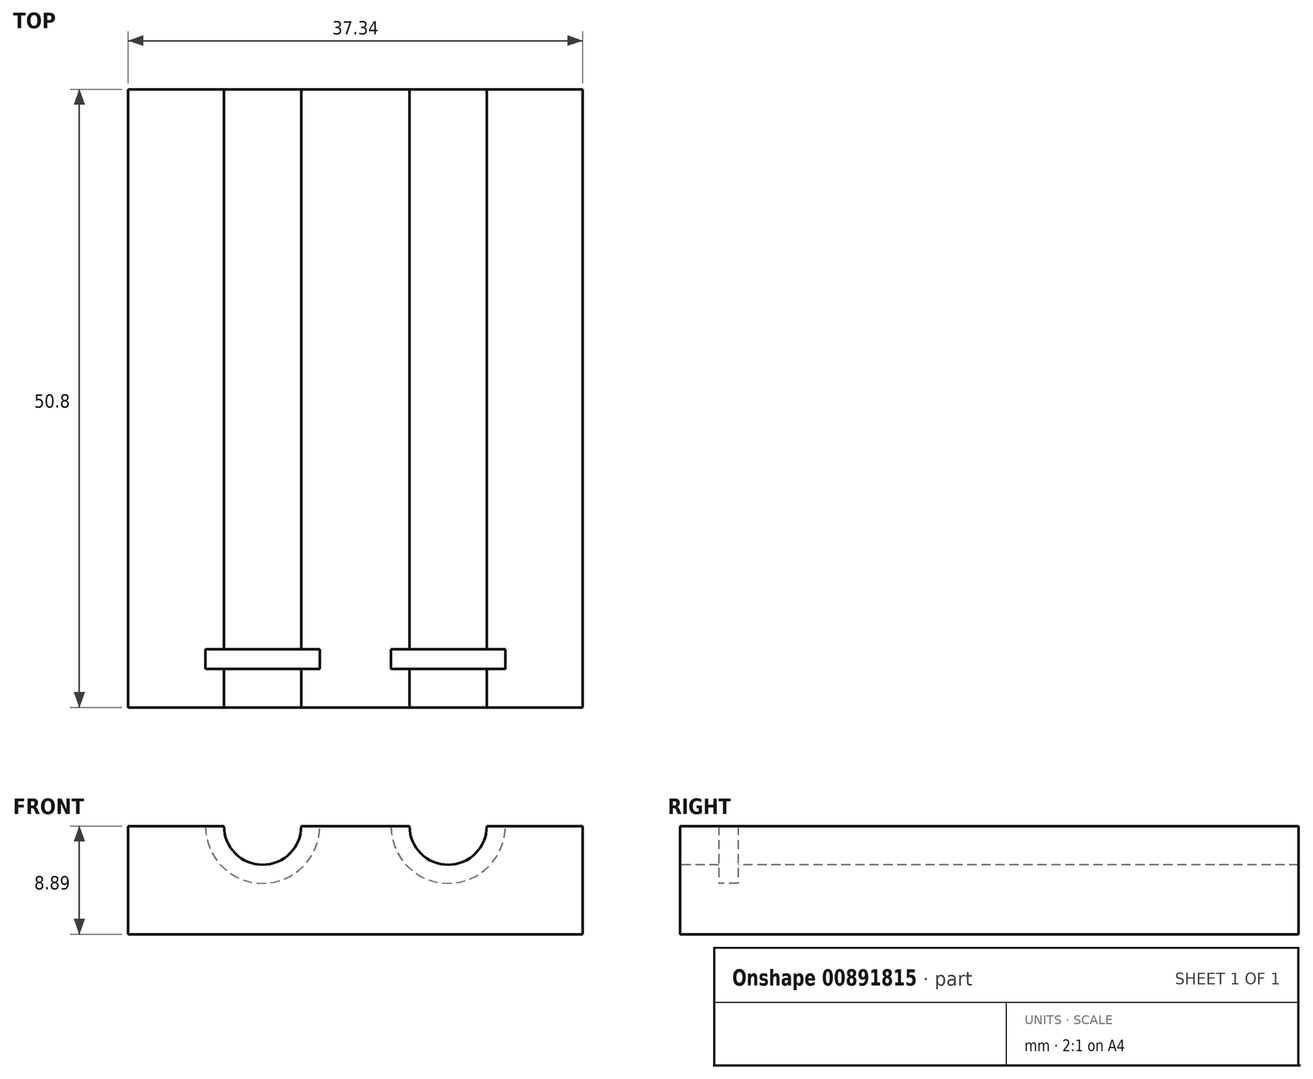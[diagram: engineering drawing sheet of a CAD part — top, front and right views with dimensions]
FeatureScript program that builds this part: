
annotation { "Feature Type Name" : "Feature", "Feature Type Description" : "" }
export const myFeature = defineFeature(function(context is Context, id is Id, definition is map)
    precondition{}
    {
        {
            assignVariable(context, id + "F0", {"name" : "padLen", "anyValue" : 1.5});
        }
        {
            var Q0;
            Q0=qCreatedBy(makeId("Front.planeOp"),FACE);
            var sketch = newSketch(context, id + "F1", { "sketchPlane" : qUnion([Q0])});
            skCircle(sketch, "E0", {"center": v(0, 0) * mm, "radius": 3.18 * mm});
            skSolve(sketch);
        }
        {
            var Q0;
            Q0 = qSketchRegion(id + "F1", true);
            extrude(context, id + "F2", {"entities" : qUnion([Q0]), "depth" : -76.2 * mm, "offsetDistance" : 25.4 * mm});
        }
        {
            var Q0;
            Q0=qCreatedBy(makeId("Front.planeOp"),FACE);
            cPlane(context, id + "F3", {"entities" : qUnion([Q0]), "cplaneType" : CPlaneType.OFFSET, "offset" : 3.17 * mm, "oppositeDirection" : true, "width" : 152.4 * mm, "height" : 152.4 * mm});
        }
        {
            var Q0;
            Q0=qCreatedBy(id+"F3.planeOp",FACE);
            var sketch = newSketch(context, id + "F4", { "sketchPlane" : qUnion([Q0])});
            skArc(sketch, "E1.0", {"start": v(-3.18, 0) * mm, "mid": v(0, -3.18) * mm, "end": v(3.18, 0) * mm});
            skArc(sketch, "E2.0", {"start": v(-4.7, 0) * mm, "mid": v(0, -4.7) * mm, "end": v(4.7, 0) * mm});
            skLineSegment(sketch, "E3", {"start": v(-3.18, 0) * mm, "end": v(-4.7, 0) * mm});
            skLineSegment(sketch, "E4", {"start": v(3.18, 0) * mm, "end": v(4.7, 0) * mm});
            skSolve(sketch);
        }
        {
            var Q0;
            Q0 = qSketchRegion(id + "F4", true);
            extrude(context, id + "F5", {"entities" : qUnion([Q0]), "operationType" : NewBodyOperationType.ADD, "oppositeDirection" : true, "depth" : (getVariable(context, 'padLen')) * mm, "offsetDistance" : 25.4 * mm});
        }
        {
            var Q0;
            Q0=makeQuery(id+"F2.opExtrude","SWEPT_BODY",BODY,{"disambiguationData":[OSD([sQuery(id+"F1.wireOp",EDGE,"E0")])]});
            transform(context, id + "F6", {"entities" : qUnion([Q0]), "transformType" : TransformType.TRANSLATION_3D, "dx" : 15.24 * mm, "dy" : 0 * mm, "dz" : 0 * mm, "makeCopy" : true});
        }
        {
            var Q0;
            Q0=qCreatedBy(makeId("Front.planeOp"),FACE);
            var sketch = newSketch(context, id + "F7", { "sketchPlane" : qUnion([Q0])});
            skLineSegment(sketch, "E5.bottom", {"start": v(-11.05, 0) * mm, "end": v(26.29, 0) * mm});
            skLineSegment(sketch, "E5.top", {"start": v(-11.05, -8.89) * mm, "end": v(26.29, -8.89) * mm});
            skLineSegment(sketch, "E5.left", {"start": v(-11.05, 0) * mm, "end": v(-11.05, -8.89) * mm});
            skLineSegment(sketch, "E5.right", {"start": v(26.29, 0) * mm, "end": v(26.29, -8.89) * mm});
            skSolve(sketch);
        }
        {
            var Q0;
            Q0 = qSketchRegion(id + "F7", true);
            extrude(context, id + "F8", {"entities" : qUnion([Q0]), "oppositeDirection" : true, "depth" : 50.8 * mm, "offsetDistance" : 25.4 * mm});
        }
        {
            var Q0;
            Q0=qCreatedBy(makeId("Front.planeOp"),FACE);
            var sketch = newSketch(context, id + "F9", { "sketchPlane" : qUnion([Q0])});
            skCircle(sketch, "E6.0", {"center": v(0, 0) * mm, "radius": 3.18 * mm});
            skCircle(sketch, "E7.0", {"center": v(15.24, 0) * mm, "radius": 3.18 * mm});
            skSolve(sketch);
        }
        {
            var Q0;
            Q0 = qSketchRegion(id + "F9", true);
            extrude(context, id + "F10", {"entities" : qUnion([Q0]), "operationType" : NewBodyOperationType.REMOVE, "endBound" : BoundingType.THROUGH_ALL, "oppositeDirection" : true, "depth" : 25.4 * mm, "offsetDistance" : 25.4 * mm});
        }
        {
            var Q0;
            Q0=qCreatedBy(id+"F3.planeOp",FACE);
            var sketch = newSketch(context, id + "F11", { "sketchPlane" : qUnion([Q0])});
            skArc(sketch, "E8.0", {"start": v(-4.7, 0) * mm, "mid": v(0, -4.7) * mm, "end": v(4.7, 0) * mm});
            skArc(sketch, "E9.0", {"start": v(-3.18, 0) * mm, "mid": v(0, -3.18) * mm, "end": v(3.18, 0) * mm});
            skArc(sketch, "E10.0", {"start": v(12.06, 0) * mm, "mid": v(15.24, -3.18) * mm, "end": v(18.41, 0) * mm});
            skArc(sketch, "E11.0", {"start": v(10.54, 0) * mm, "mid": v(15.24, -4.7) * mm, "end": v(19.94, 0) * mm});
            skLineSegment(sketch, "E12", {"start": v(-4.7, 0) * mm, "end": v(-3.18, 0) * mm});
            skLineSegment(sketch, "E13", {"start": v(4.7, 0) * mm, "end": v(3.18, 0) * mm});
            skLineSegment(sketch, "E14", {"start": v(10.54, 0) * mm, "end": v(12.06, 0) * mm});
            skLineSegment(sketch, "E15", {"start": v(19.94, 0) * mm, "end": v(18.41, 0) * mm});
            skSolve(sketch);
        }
        {
            var Q0;
            Q0 = qSketchRegion(id + "F11", true);
            extrude(context, id + "F12", {"entities" : qUnion([Q0]), "operationType" : NewBodyOperationType.REMOVE, "oppositeDirection" : true, "depth" : (getVariable(context, 'padLen') + 0.1) * mm, "offsetDistance" : 25.4 * mm});
        }
    });
